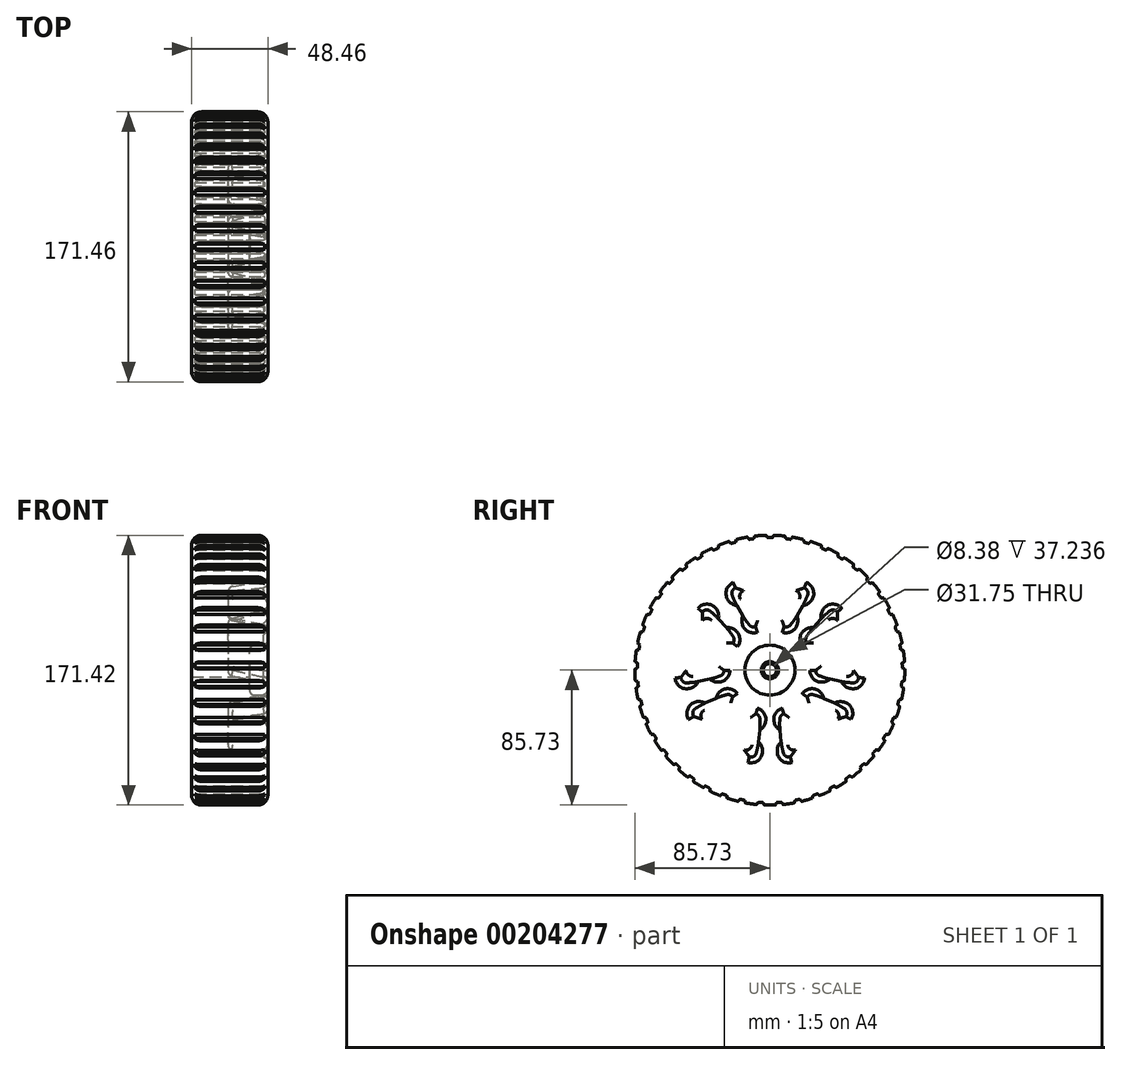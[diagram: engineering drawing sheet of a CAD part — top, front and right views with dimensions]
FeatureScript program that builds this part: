
annotation { "Feature Type Name" : "Feature", "Feature Type Description" : "" }
export const myFeature = defineFeature(function(context is Context, id is Id, definition is map)
    precondition{}
    {
        {
            var Q0;
            Q0=qCreatedBy(makeId("Front.planeOp"),FACE);
            var sketch = newSketch(context, id + "F0", { "sketchPlane" : qUnion([Q0])});
            skLineSegment(sketch, "E0", {"start": v(0, 85.73) * mm, "end": v(17.78, 85.73) * mm});
            skLineSegment(sketch, "E1", {"start": v(24.13, 79.38) * mm, "end": v(24.13, 19.05) * mm});
            skLineSegment(sketch, "E2", {"start": v(20.96, 15.88) * mm, "end": v(15.67, 15.88) * mm});
            skLineSegment(sketch, "E3", {"start": v(12.5, 12.7) * mm, "end": v(12.5, 5.46) * mm});
            skLineSegment(sketch, "E4", {"start": v(27.52, 0) * mm, "end": v(-27.22, 0) * mm});
            skLineSegment(sketch, "E5", {"start": v(0, 85.73) * mm, "end": v(-17.98, 85.73) * mm});
            skLineSegment(sketch, "E6", {"start": v(-24.33, 79.38) * mm, "end": v(-24.33, 4.2) * mm});
            skLineSegment(sketch, "E7", {"start": v(-24.33, 4.2) * mm, "end": v(12.9, 4.2) * mm});
            skPoint(sketch, "E8.end.orphan", {"position": v(0, 7.03) * mm});
            skLineSegment(sketch, "E9", {"start": v(12.5, 5.46) * mm, "end": v(12.9, 5.46) * mm});
            skLineSegment(sketch, "E10", {"start": v(12.9, 5.46) * mm, "end": v(12.9, 4.2) * mm});
            skPoint(sketch, "E11.visualSharp", {"position": v(-24.33, 85.73) * mm});
            skArc(sketch, "E11.filletArc", {"start": v(-17.98, 85.73) * mm, "mid": v(-22.47, 83.87) * mm, "end": v(-24.33, 79.38) * mm});
            skPoint(sketch, "E12.visualSharp", {"position": v(24.13, 85.73) * mm});
            skArc(sketch, "E12.filletArc", {"start": v(24.13, 79.38) * mm, "mid": v(22.27, 83.87) * mm, "end": v(17.78, 85.73) * mm});
            skPoint(sketch, "E13.visualSharp", {"position": v(24.13, 15.88) * mm});
            skArc(sketch, "E13.filletArc", {"start": v(20.96, 15.88) * mm, "mid": v(23.2, 16.8) * mm, "end": v(24.13, 19.05) * mm});
            skPoint(sketch, "E14.visualSharp", {"position": v(12.5, 15.88) * mm});
            skArc(sketch, "E14.filletArc", {"start": v(15.67, 15.88) * mm, "mid": v(13.43, 14.95) * mm, "end": v(12.5, 12.7) * mm});
            skSolve(sketch);
        }
        {
            var Q0;
            Q0=makeQuery(id+"F0.imprint","IMPRINT",FACE,{"disambiguationData":[TD([[makeQuery(id+"F0.imprint","IMPRINT",EDGE,{"derivedFrom":sQuery(id+"F0.wireOp",EDGE,"E0")}),-1.0]])]});
            var Q1;
            Q1=sQuery(id+"F0.wireOp",EDGE,"E4");
            revolve(context, id + "F1", {"entities" : qUnion([Q0]), "axis" : qUnion([Q1]), "revolveType" : RevolveType.FULL});
        }
        {
            var Q0;
            Q0=makeQuery(id+"F1.opRevolve","SWEPT_FACE",FACE,{"disambiguationData":[OSD([sQuery(id+"F0.wireOp",EDGE,"E1")])]});
            var sketch = newSketch(context, id + "F2", { "sketchPlane" : qUnion([Q0])});
            skArc(sketch, "E15", {"start": v(12.14, 25.87) * mm, "mid": v(0, 28.58) * mm, "end": v(-12.14, 25.87) * mm});
            skArc(sketch, "E16", {"start": v(26.46, 50.66) * mm, "mid": v(0, 57.15) * mm, "end": v(-26.46, 50.66) * mm});
            skLineSegment(sketch, "E17", {"start": v(-12.14, 25.87) * mm, "end": v(-26.46, 50.66) * mm});
            skLineSegment(sketch, "E18", {"start": v(12.14, 25.87) * mm, "end": v(26.46, 50.66) * mm});
            skPoint(sketch, "E19.visualSharp", {"position": v(-26.46, 50.66) * mm});
            skPoint(sketch, "E20.visualSharp", {"position": v(26.46, 50.66) * mm});
            skPoint(sketch, "E21.visualSharp", {"position": v(12.14, 25.87) * mm});
            skPoint(sketch, "E22.visualSharp", {"position": v(-12.14, 25.87) * mm});
            skLineSegment(sketch, "E23.1.0", {"start": v(-28.35, -3.56) * mm, "end": v(-56.35, -9.5) * mm});
            skArc(sketch, "E23.1.1", {"start": v(-40, 40.82) * mm, "mid": v(-54.35, 17.66) * mm, "end": v(-56.35, -9.5) * mm});
            skLineSegment(sketch, "E23.1.2", {"start": v(-20.85, 19.54) * mm, "end": v(-40, 40.82) * mm});
            skArc(sketch, "E23.1.3", {"start": v(-20.85, 19.54) * mm, "mid": v(-27.18, 8.83) * mm, "end": v(-28.35, -3.56) * mm});
            skLineSegment(sketch, "E23.2.0", {"start": v(-5.38, -28.06) * mm, "end": v(-8.37, -56.53) * mm});
            skArc(sketch, "E23.2.1", {"start": v(-51.18, -25.43) * mm, "mid": v(-33.6, -46.24) * mm, "end": v(-8.37, -56.53) * mm});
            skLineSegment(sketch, "E23.2.2", {"start": v(-25.03, -13.79) * mm, "end": v(-51.18, -25.43) * mm});
            skArc(sketch, "E23.2.3", {"start": v(-25.03, -13.79) * mm, "mid": v(-16.8, -23.12) * mm, "end": v(-5.38, -28.06) * mm});
            skLineSegment(sketch, "E23.3.0", {"start": v(25.03, -13.79) * mm, "end": v(51.18, -25.43) * mm});
            skArc(sketch, "E23.3.1", {"start": v(8.37, -56.53) * mm, "mid": v(33.6, -46.24) * mm, "end": v(51.18, -25.43) * mm});
            skLineSegment(sketch, "E23.3.2", {"start": v(5.38, -28.06) * mm, "end": v(8.37, -56.53) * mm});
            skArc(sketch, "E23.3.3", {"start": v(5.38, -28.06) * mm, "mid": v(16.8, -23.12) * mm, "end": v(25.03, -13.79) * mm});
            skLineSegment(sketch, "E23.4.0", {"start": v(20.85, 19.54) * mm, "end": v(40, 40.82) * mm});
            skArc(sketch, "E23.4.1", {"start": v(56.35, -9.5) * mm, "mid": v(54.35, 17.66) * mm, "end": v(40, 40.82) * mm});
            skLineSegment(sketch, "E23.4.2", {"start": v(28.35, -3.56) * mm, "end": v(56.35, -9.5) * mm});
            skArc(sketch, "E23.4.3", {"start": v(28.35, -3.56) * mm, "mid": v(27.18, 8.83) * mm, "end": v(20.85, 19.54) * mm});
            skSolve(sketch);
        }
        {
            var Q0;
            Q0=qSketchRegion(id+"F2",true);
            extrude(context, id + "F3", {"entities" : qUnion([Q0]), "operationType" : NewBodyOperationType.REMOVE, "oppositeDirection" : true, "depth" : 25.4 * mm, "hasDraft" : true, "draftAngle" : 10 * degree, "draftPullDirection" : true});
        }
        {
            var Q0;
            Q0=makeQuery(id+"F3.boolean.opBoolean","COPY",FACE,{"derivedFrom":makeQuery(id+"F3.opExtrude","SWEPT_FACE",FACE,{"disambiguationData":[OSD([sQuery(id+"F2.wireOp",EDGE,"E16")])]})});
            var Q1;
            Q1=makeQuery(id+"F3.boolean.opBoolean","COPY",FACE,{"derivedFrom":makeQuery(id+"F3.opExtrude","SWEPT_FACE",FACE,{"disambiguationData":[OSD([sQuery(id+"F2.wireOp",EDGE,"E15")])]})});
            var Q2;
            Q2=makeQuery(id+"F3.boolean.opBoolean","COPY",FACE,{"derivedFrom":makeQuery(id+"F3.opExtrude","CAP_FACE",FACE,{"disambiguationData":[OSD([sQuery(id+"F2.wireOp",EDGE,"E15"),sQuery(id+"F2.wireOp",EDGE,"E16"),sQuery(id+"F2.wireOp",EDGE,"E17"),sQuery(id+"F2.wireOp",EDGE,"E18")])],"isStart":false})});
            var Q3;
            Q3=makeQuery(id+"F3.boolean.opBoolean","COPY",FACE,{"derivedFrom":makeQuery(id+"F3.opExtrude","CAP_FACE",FACE,{"disambiguationData":[OSD([sQuery(id+"F2.wireOp",EDGE,"E23.1.0"),sQuery(id+"F2.wireOp",EDGE,"E23.1.1"),sQuery(id+"F2.wireOp",EDGE,"E23.1.2"),sQuery(id+"F2.wireOp",EDGE,"E23.1.3")])],"isStart":false})});
            var Q4;
            Q4=makeQuery(id+"F3.boolean.opBoolean","COPY",FACE,{"derivedFrom":makeQuery(id+"F3.opExtrude","SWEPT_FACE",FACE,{"disambiguationData":[OSD([sQuery(id+"F2.wireOp",EDGE,"E23.1.1")])]})});
            var Q5;
            Q5=makeQuery(id+"F3.boolean.opBoolean","COPY",FACE,{"derivedFrom":makeQuery(id+"F3.opExtrude","SWEPT_FACE",FACE,{"disambiguationData":[OSD([sQuery(id+"F2.wireOp",EDGE,"E23.1.3")])]})});
            var Q6;
            Q6=makeQuery(id+"F3.boolean.opBoolean","COPY",FACE,{"derivedFrom":makeQuery(id+"F3.opExtrude","CAP_FACE",FACE,{"disambiguationData":[OSD([sQuery(id+"F2.wireOp",EDGE,"E23.3.0"),sQuery(id+"F2.wireOp",EDGE,"E23.3.1"),sQuery(id+"F2.wireOp",EDGE,"E23.3.2"),sQuery(id+"F2.wireOp",EDGE,"E23.3.3")])],"isStart":false})});
            var Q7;
            Q7=makeQuery(id+"F3.boolean.opBoolean","COPY",FACE,{"derivedFrom":makeQuery(id+"F3.opExtrude","CAP_FACE",FACE,{"disambiguationData":[OSD([sQuery(id+"F2.wireOp",EDGE,"E23.2.0"),sQuery(id+"F2.wireOp",EDGE,"E23.2.1"),sQuery(id+"F2.wireOp",EDGE,"E23.2.2"),sQuery(id+"F2.wireOp",EDGE,"E23.2.3")])],"isStart":false})});
            var Q8;
            Q8=makeQuery(id+"F3.boolean.opBoolean","COPY",FACE,{"derivedFrom":makeQuery(id+"F3.opExtrude","SWEPT_FACE",FACE,{"disambiguationData":[OSD([sQuery(id+"F2.wireOp",EDGE,"E23.2.3")])]})});
            var Q9;
            Q9=makeQuery(id+"F3.boolean.opBoolean","COPY",FACE,{"derivedFrom":makeQuery(id+"F3.opExtrude","SWEPT_FACE",FACE,{"disambiguationData":[OSD([sQuery(id+"F2.wireOp",EDGE,"E23.3.3")])]})});
            var Q10;
            Q10=makeQuery(id+"F3.boolean.opBoolean","COPY",FACE,{"derivedFrom":makeQuery(id+"F3.opExtrude","SWEPT_FACE",FACE,{"disambiguationData":[OSD([sQuery(id+"F2.wireOp",EDGE,"E23.4.3")])]})});
            var Q11;
            Q11=makeQuery(id+"F3.boolean.opBoolean","COPY",FACE,{"derivedFrom":makeQuery(id+"F3.opExtrude","CAP_FACE",FACE,{"disambiguationData":[OSD([sQuery(id+"F2.wireOp",EDGE,"E23.4.0"),sQuery(id+"F2.wireOp",EDGE,"E23.4.1"),sQuery(id+"F2.wireOp",EDGE,"E23.4.2"),sQuery(id+"F2.wireOp",EDGE,"E23.4.3")])],"isStart":false})});
            var Q12;
            Q12=makeQuery(id+"F3.boolean.opBoolean","COPY",FACE,{"derivedFrom":makeQuery(id+"F3.opExtrude","SWEPT_FACE",FACE,{"disambiguationData":[OSD([sQuery(id+"F2.wireOp",EDGE,"E23.4.1")])]})});
            var Q13;
            Q13=makeQuery(id+"F3.boolean.opBoolean","COPY",FACE,{"derivedFrom":makeQuery(id+"F3.opExtrude","SWEPT_FACE",FACE,{"disambiguationData":[OSD([sQuery(id+"F2.wireOp",EDGE,"E23.3.1")])]})});
            var Q14;
            Q14=makeQuery(id+"F3.boolean.opBoolean","COPY",FACE,{"derivedFrom":makeQuery(id+"F3.opExtrude","SWEPT_FACE",FACE,{"disambiguationData":[OSD([sQuery(id+"F2.wireOp",EDGE,"E23.2.1")])]})});
            fillet(context, id + "F4", {"entities" : qUnion([Q0, Q1, Q2, Q3, Q4, Q5, Q6, Q7, Q8, Q9, Q10, Q11, Q12, Q13, Q14]), "radius" : 3.8 * mm, "tangentPropagation" : true, "allowEdgeOverflow" : false});
        }
        {
            var Q0;
            Q0=qCreatedBy(makeId("Right.planeOp"),FACE);
            var sketch = newSketch(context, id + "F5", { "sketchPlane" : qUnion([Q0])});
            skLineSegment(sketch, "E24", {"start": v(-1.59, 84.14) * mm, "end": v(1.59, 84.14) * mm});
            skLineSegment(sketch, "E25", {"start": v(-1.59, 84.14) * mm, "end": v(-3.18, 87.34) * mm});
            skLineSegment(sketch, "E26", {"start": v(1.59, 84.14) * mm, "end": v(3.17, 87.34) * mm});
            skLineSegment(sketch, "E27", {"start": v(-3.18, 87.34) * mm, "end": v(3.18, 87.34) * mm});
            skLineSegment(sketch, "E28.1.0", {"start": v(-15.3, 86.05) * mm, "end": v(-9.01, 86.94) * mm});
            skLineSegment(sketch, "E28.1.1", {"start": v(-13.28, 83.1) * mm, "end": v(-10.14, 83.54) * mm});
            skLineSegment(sketch, "E28.1.2", {"start": v(-10.14, 83.54) * mm, "end": v(-9.01, 86.94) * mm});
            skLineSegment(sketch, "E28.1.3", {"start": v(-13.28, 83.1) * mm, "end": v(-15.3, 86.05) * mm});
            skLineSegment(sketch, "E28.2.0", {"start": v(-27.13, 83.09) * mm, "end": v(-21.02, 84.84) * mm});
            skLineSegment(sketch, "E28.2.1", {"start": v(-24.72, 80.44) * mm, "end": v(-21.67, 81.32) * mm});
            skLineSegment(sketch, "E28.2.2", {"start": v(-21.67, 81.32) * mm, "end": v(-21.02, 84.84) * mm});
            skLineSegment(sketch, "E28.2.3", {"start": v(-24.72, 80.44) * mm, "end": v(-27.13, 83.09) * mm});
            skLineSegment(sketch, "E28.3.0", {"start": v(-38.43, 78.5) * mm, "end": v(-32.63, 81.08) * mm});
            skLineSegment(sketch, "E28.3.1", {"start": v(-35.67, 76.22) * mm, "end": v(-32.77, 77.5) * mm});
            skLineSegment(sketch, "E28.3.2", {"start": v(-32.77, 77.5) * mm, "end": v(-32.63, 81.08) * mm});
            skLineSegment(sketch, "E28.3.3", {"start": v(-35.67, 76.22) * mm, "end": v(-38.43, 78.5) * mm});
            skLineSegment(sketch, "E28.4.0", {"start": v(-48.98, 72.4) * mm, "end": v(-43.6, 75.76) * mm});
            skLineSegment(sketch, "E28.4.1", {"start": v(-45.93, 70.51) * mm, "end": v(-43.24, 72.2) * mm});
            skLineSegment(sketch, "E28.4.2", {"start": v(-43.24, 72.2) * mm, "end": v(-43.6, 75.76) * mm});
            skLineSegment(sketch, "E28.4.3", {"start": v(-45.93, 70.51) * mm, "end": v(-48.98, 72.4) * mm});
            skLineSegment(sketch, "E28.5.0", {"start": v(-58.58, 64.87) * mm, "end": v(-53.71, 68.95) * mm});
            skLineSegment(sketch, "E28.5.1", {"start": v(-55.3, 63.43) * mm, "end": v(-52.87, 65.47) * mm});
            skLineSegment(sketch, "E28.5.2", {"start": v(-52.87, 65.47) * mm, "end": v(-53.71, 68.95) * mm});
            skLineSegment(sketch, "E28.5.3", {"start": v(-55.3, 63.43) * mm, "end": v(-58.58, 64.87) * mm});
            skLineSegment(sketch, "E28.6.0", {"start": v(-67.03, 56.09) * mm, "end": v(-62.79, 60.8) * mm});
            skLineSegment(sketch, "E28.6.1", {"start": v(-63.59, 55.12) * mm, "end": v(-61.46, 57.48) * mm});
            skLineSegment(sketch, "E28.6.2", {"start": v(-61.46, 57.48) * mm, "end": v(-62.79, 60.8) * mm});
            skLineSegment(sketch, "E28.6.3", {"start": v(-63.59, 55.12) * mm, "end": v(-67.03, 56.09) * mm});
            skLineSegment(sketch, "E28.7.0", {"start": v(-74.19, 46.21) * mm, "end": v(-70.64, 51.47) * mm});
            skLineSegment(sketch, "E28.7.1", {"start": v(-70.64, 45.73) * mm, "end": v(-68.87, 48.37) * mm});
            skLineSegment(sketch, "E28.7.2", {"start": v(-68.87, 48.37) * mm, "end": v(-70.64, 51.47) * mm});
            skLineSegment(sketch, "E28.7.3", {"start": v(-70.64, 45.73) * mm, "end": v(-74.19, 46.21) * mm});
            skLineSegment(sketch, "E28.8.0", {"start": v(-79.9, 35.44) * mm, "end": v(-77.11, 41.14) * mm});
            skLineSegment(sketch, "E28.8.1", {"start": v(-76.32, 35.46) * mm, "end": v(-74.93, 38.31) * mm});
            skLineSegment(sketch, "E28.8.2", {"start": v(-74.93, 38.31) * mm, "end": v(-77.11, 41.14) * mm});
            skLineSegment(sketch, "E28.8.3", {"start": v(-76.32, 35.46) * mm, "end": v(-79.9, 35.44) * mm});
            skLineSegment(sketch, "E28.9.0", {"start": v(-84.05, 23.97) * mm, "end": v(-82.09, 30.01) * mm});
            skLineSegment(sketch, "E28.9.1", {"start": v(-80.51, 24.5) * mm, "end": v(-79.53, 27.5) * mm});
            skLineSegment(sketch, "E28.9.2", {"start": v(-79.53, 27.5) * mm, "end": v(-82.09, 30.01) * mm});
            skLineSegment(sketch, "E28.9.3", {"start": v(-80.51, 24.5) * mm, "end": v(-84.05, 23.97) * mm});
            skLineSegment(sketch, "E28.10.0", {"start": v(-86.57, 12.04) * mm, "end": v(-85.47, 18.3) * mm});
            skLineSegment(sketch, "E28.10.1", {"start": v(-83.13, 13.05) * mm, "end": v(-82.58, 16.17) * mm});
            skLineSegment(sketch, "E28.10.2", {"start": v(-82.58, 16.17) * mm, "end": v(-85.47, 18.3) * mm});
            skLineSegment(sketch, "E28.10.3", {"start": v(-83.13, 13.05) * mm, "end": v(-86.57, 12.04) * mm});
            skLineSegment(sketch, "E28.11.0", {"start": v(-87.4, -0.12) * mm, "end": v(-87.18, 6.22) * mm});
            skLineSegment(sketch, "E28.11.1", {"start": v(-84.14, 1.35) * mm, "end": v(-84.03, 4.52) * mm});
            skLineSegment(sketch, "E28.11.2", {"start": v(-84.03, 4.52) * mm, "end": v(-87.18, 6.22) * mm});
            skLineSegment(sketch, "E28.11.3", {"start": v(-84.14, 1.35) * mm, "end": v(-87.4, -0.12) * mm});
            skLineSegment(sketch, "E28.12.0", {"start": v(-86.53, -12.29) * mm, "end": v(-87.2, -5.97) * mm});
            skLineSegment(sketch, "E28.12.1", {"start": v(-83.51, -10.37) * mm, "end": v(-83.84, -7.22) * mm});
            skLineSegment(sketch, "E28.12.2", {"start": v(-83.84, -7.22) * mm, "end": v(-87.2, -5.97) * mm});
            skLineSegment(sketch, "E28.12.3", {"start": v(-83.51, -10.37) * mm, "end": v(-86.53, -12.29) * mm});
            skLineSegment(sketch, "E28.13.0", {"start": v(-83.98, -24.21) * mm, "end": v(-85.52, -18.05) * mm});
            skLineSegment(sketch, "E28.13.1", {"start": v(-81.25, -21.9) * mm, "end": v(-82.02, -18.81) * mm});
            skLineSegment(sketch, "E28.13.2", {"start": v(-82.02, -18.81) * mm, "end": v(-85.52, -18.05) * mm});
            skLineSegment(sketch, "E28.13.3", {"start": v(-81.25, -21.9) * mm, "end": v(-83.98, -24.21) * mm});
            skLineSegment(sketch, "E28.14.0", {"start": v(-79.8, -35.66) * mm, "end": v(-82.17, -29.78) * mm});
            skLineSegment(sketch, "E28.14.1", {"start": v(-77.42, -33) * mm, "end": v(-78.6, -30.05) * mm});
            skLineSegment(sketch, "E28.14.2", {"start": v(-78.6, -30.05) * mm, "end": v(-82.17, -29.78) * mm});
            skLineSegment(sketch, "E28.14.3", {"start": v(-77.42, -33) * mm, "end": v(-79.8, -35.66) * mm});
            skLineSegment(sketch, "E28.15.0", {"start": v(-74.06, -46.42) * mm, "end": v(-77.23, -40.92) * mm});
            skLineSegment(sketch, "E28.15.1", {"start": v(-72.07, -43.44) * mm, "end": v(-73.66, -40.7) * mm});
            skLineSegment(sketch, "E28.15.2", {"start": v(-73.66, -40.7) * mm, "end": v(-77.23, -40.92) * mm});
            skLineSegment(sketch, "E28.15.3", {"start": v(-72.07, -43.44) * mm, "end": v(-74.06, -46.42) * mm});
            skLineSegment(sketch, "E28.16.0", {"start": v(-66.87, -56.28) * mm, "end": v(-70.78, -51.27) * mm});
            skLineSegment(sketch, "E28.16.1", {"start": v(-65.32, -53.05) * mm, "end": v(-67.28, -50.55) * mm});
            skLineSegment(sketch, "E28.16.2", {"start": v(-67.28, -50.55) * mm, "end": v(-70.78, -51.27) * mm});
            skLineSegment(sketch, "E28.16.3", {"start": v(-65.32, -53.05) * mm, "end": v(-66.87, -56.28) * mm});
            skLineSegment(sketch, "E28.17.0", {"start": v(-58.4, -65.04) * mm, "end": v(-62.96, -60.63) * mm});
            skLineSegment(sketch, "E28.17.1", {"start": v(-57.3, -61.63) * mm, "end": v(-59.59, -59.42) * mm});
            skLineSegment(sketch, "E28.17.2", {"start": v(-59.59, -59.42) * mm, "end": v(-62.96, -60.63) * mm});
            skLineSegment(sketch, "E28.17.3", {"start": v(-57.3, -61.63) * mm, "end": v(-58.4, -65.04) * mm});
            skLineSegment(sketch, "E28.18.0", {"start": v(-48.77, -72.53) * mm, "end": v(-53.9, -68.8) * mm});
            skLineSegment(sketch, "E28.18.1", {"start": v(-48.17, -69) * mm, "end": v(-50.74, -67.14) * mm});
            skLineSegment(sketch, "E28.18.2", {"start": v(-50.74, -67.14) * mm, "end": v(-53.9, -68.8) * mm});
            skLineSegment(sketch, "E28.18.3", {"start": v(-48.17, -69) * mm, "end": v(-48.77, -72.53) * mm});
            skLineSegment(sketch, "E28.19.0", {"start": v(-38.2, -78.61) * mm, "end": v(-43.8, -75.63) * mm});
            skLineSegment(sketch, "E28.19.1", {"start": v(-38.1, -75.03) * mm, "end": v(-40.9, -73.54) * mm});
            skLineSegment(sketch, "E28.19.2", {"start": v(-40.9, -73.54) * mm, "end": v(-43.8, -75.63) * mm});
            skLineSegment(sketch, "E28.19.3", {"start": v(-38.1, -75.03) * mm, "end": v(-38.2, -78.61) * mm});
            skLineSegment(sketch, "E28.20.0", {"start": v(-26.9, -83.16) * mm, "end": v(-32.86, -81) * mm});
            skLineSegment(sketch, "E28.20.1", {"start": v(-27.28, -79.6) * mm, "end": v(-30.27, -78.52) * mm});
            skLineSegment(sketch, "E28.20.2", {"start": v(-30.27, -78.52) * mm, "end": v(-32.86, -81) * mm});
            skLineSegment(sketch, "E28.20.3", {"start": v(-27.28, -79.6) * mm, "end": v(-26.9, -83.16) * mm});
            skLineSegment(sketch, "E28.21.0", {"start": v(-15.05, -86.1) * mm, "end": v(-21.27, -84.78) * mm});
            skLineSegment(sketch, "E28.21.1", {"start": v(-15.94, -82.63) * mm, "end": v(-19.05, -81.97) * mm});
            skLineSegment(sketch, "E28.21.2", {"start": v(-19.05, -81.97) * mm, "end": v(-21.27, -84.78) * mm});
            skLineSegment(sketch, "E28.21.3", {"start": v(-15.94, -82.63) * mm, "end": v(-15.05, -86.1) * mm});
            skLineSegment(sketch, "E28.22.0", {"start": v(-2.93, -87.35) * mm, "end": v(-9.26, -86.91) * mm});
            skLineSegment(sketch, "E28.22.1", {"start": v(-4.29, -84.04) * mm, "end": v(-7.45, -83.82) * mm});
            skLineSegment(sketch, "E28.22.2", {"start": v(-7.45, -83.82) * mm, "end": v(-9.26, -86.91) * mm});
            skLineSegment(sketch, "E28.22.3", {"start": v(-4.29, -84.04) * mm, "end": v(-2.93, -87.35) * mm});
            skLineSegment(sketch, "E28.23.0", {"start": v(9.26, -86.91) * mm, "end": v(2.93, -87.35) * mm});
            skLineSegment(sketch, "E28.23.1", {"start": v(7.45, -83.82) * mm, "end": v(4.29, -84.04) * mm});
            skLineSegment(sketch, "E28.23.2", {"start": v(4.29, -84.04) * mm, "end": v(2.93, -87.35) * mm});
            skLineSegment(sketch, "E28.23.3", {"start": v(7.45, -83.82) * mm, "end": v(9.26, -86.91) * mm});
            skLineSegment(sketch, "E28.24.0", {"start": v(21.27, -84.78) * mm, "end": v(15.05, -86.1) * mm});
            skLineSegment(sketch, "E28.24.1", {"start": v(19.05, -81.97) * mm, "end": v(15.94, -82.63) * mm});
            skLineSegment(sketch, "E28.24.2", {"start": v(15.94, -82.63) * mm, "end": v(15.05, -86.1) * mm});
            skLineSegment(sketch, "E28.24.3", {"start": v(19.05, -81.97) * mm, "end": v(21.27, -84.78) * mm});
            skPoint(sketch, "E28.center", {"position": v(0, 0) * mm});
            skLineSegment(sketch, "E29.1.25.0", {"start": v(32.86, -81) * mm, "end": v(26.9, -83.16) * mm});
            skLineSegment(sketch, "E29.3.25.0", {"start": v(30.27, -78.52) * mm, "end": v(27.28, -79.6) * mm});
            skLineSegment(sketch, "E29.6.25.0", {"start": v(27.28, -79.6) * mm, "end": v(26.9, -83.16) * mm});
            skLineSegment(sketch, "E29.9.25.0", {"start": v(30.27, -78.52) * mm, "end": v(32.86, -81) * mm});
            skLineSegment(sketch, "E29.1.26.0", {"start": v(43.8, -75.63) * mm, "end": v(38.2, -78.61) * mm});
            skLineSegment(sketch, "E29.3.26.0", {"start": v(40.9, -73.54) * mm, "end": v(38.1, -75.03) * mm});
            skLineSegment(sketch, "E29.6.26.0", {"start": v(38.1, -75.03) * mm, "end": v(38.2, -78.61) * mm});
            skLineSegment(sketch, "E29.9.26.0", {"start": v(40.9, -73.54) * mm, "end": v(43.8, -75.63) * mm});
            skLineSegment(sketch, "E29.1.27.0", {"start": v(53.9, -68.8) * mm, "end": v(48.77, -72.53) * mm});
            skLineSegment(sketch, "E29.3.27.0", {"start": v(50.74, -67.14) * mm, "end": v(48.17, -69) * mm});
            skLineSegment(sketch, "E29.6.27.0", {"start": v(48.17, -69) * mm, "end": v(48.77, -72.53) * mm});
            skLineSegment(sketch, "E29.9.27.0", {"start": v(50.74, -67.14) * mm, "end": v(53.9, -68.8) * mm});
            skLineSegment(sketch, "E29.1.28.0", {"start": v(62.96, -60.63) * mm, "end": v(58.4, -65.04) * mm});
            skLineSegment(sketch, "E29.3.28.0", {"start": v(59.59, -59.42) * mm, "end": v(57.3, -61.63) * mm});
            skLineSegment(sketch, "E29.6.28.0", {"start": v(57.3, -61.63) * mm, "end": v(58.4, -65.04) * mm});
            skLineSegment(sketch, "E29.9.28.0", {"start": v(59.59, -59.42) * mm, "end": v(62.96, -60.63) * mm});
            skLineSegment(sketch, "E29.1.29.0", {"start": v(70.78, -51.27) * mm, "end": v(66.87, -56.28) * mm});
            skLineSegment(sketch, "E29.3.29.0", {"start": v(67.28, -50.55) * mm, "end": v(65.32, -53.05) * mm});
            skLineSegment(sketch, "E29.6.29.0", {"start": v(65.32, -53.05) * mm, "end": v(66.87, -56.28) * mm});
            skLineSegment(sketch, "E29.9.29.0", {"start": v(67.28, -50.55) * mm, "end": v(70.78, -51.27) * mm});
            skLineSegment(sketch, "E29.1.30.0", {"start": v(77.23, -40.92) * mm, "end": v(74.06, -46.42) * mm});
            skLineSegment(sketch, "E29.3.30.0", {"start": v(73.66, -40.7) * mm, "end": v(72.07, -43.44) * mm});
            skLineSegment(sketch, "E29.6.30.0", {"start": v(72.07, -43.44) * mm, "end": v(74.06, -46.42) * mm});
            skLineSegment(sketch, "E29.9.30.0", {"start": v(73.66, -40.7) * mm, "end": v(77.23, -40.92) * mm});
            skLineSegment(sketch, "E29.1.31.0", {"start": v(82.17, -29.78) * mm, "end": v(79.8, -35.66) * mm});
            skLineSegment(sketch, "E29.3.31.0", {"start": v(78.6, -30.05) * mm, "end": v(77.42, -33) * mm});
            skLineSegment(sketch, "E29.6.31.0", {"start": v(77.42, -33) * mm, "end": v(79.8, -35.66) * mm});
            skLineSegment(sketch, "E29.9.31.0", {"start": v(78.6, -30.05) * mm, "end": v(82.17, -29.78) * mm});
            skLineSegment(sketch, "E29.1.32.0", {"start": v(85.52, -18.05) * mm, "end": v(83.98, -24.21) * mm});
            skLineSegment(sketch, "E29.3.32.0", {"start": v(82.02, -18.81) * mm, "end": v(81.25, -21.9) * mm});
            skLineSegment(sketch, "E29.6.32.0", {"start": v(81.25, -21.9) * mm, "end": v(83.98, -24.21) * mm});
            skLineSegment(sketch, "E29.9.32.0", {"start": v(82.02, -18.81) * mm, "end": v(85.52, -18.05) * mm});
            skLineSegment(sketch, "E29.1.33.0", {"start": v(87.2, -5.97) * mm, "end": v(86.53, -12.29) * mm});
            skLineSegment(sketch, "E29.3.33.0", {"start": v(83.84, -7.22) * mm, "end": v(83.51, -10.37) * mm});
            skLineSegment(sketch, "E29.6.33.0", {"start": v(83.51, -10.37) * mm, "end": v(86.53, -12.29) * mm});
            skLineSegment(sketch, "E29.9.33.0", {"start": v(83.84, -7.22) * mm, "end": v(87.2, -5.97) * mm});
            skLineSegment(sketch, "E29.1.34.0", {"start": v(87.18, 6.22) * mm, "end": v(87.4, -0.12) * mm});
            skLineSegment(sketch, "E29.3.34.0", {"start": v(84.03, 4.52) * mm, "end": v(84.14, 1.35) * mm});
            skLineSegment(sketch, "E29.6.34.0", {"start": v(84.14, 1.35) * mm, "end": v(87.4, -0.12) * mm});
            skLineSegment(sketch, "E29.9.34.0", {"start": v(84.03, 4.52) * mm, "end": v(87.18, 6.22) * mm});
            skLineSegment(sketch, "E30.1.35.0", {"start": v(85.47, 18.3) * mm, "end": v(86.57, 12.04) * mm});
            skLineSegment(sketch, "E30.3.35.0", {"start": v(82.58, 16.17) * mm, "end": v(83.13, 13.05) * mm});
            skLineSegment(sketch, "E30.6.35.0", {"start": v(83.13, 13.05) * mm, "end": v(86.57, 12.04) * mm});
            skLineSegment(sketch, "E30.9.35.0", {"start": v(82.58, 16.17) * mm, "end": v(85.47, 18.3) * mm});
            skLineSegment(sketch, "E30.1.36.0", {"start": v(82.09, 30.01) * mm, "end": v(84.05, 23.97) * mm});
            skLineSegment(sketch, "E30.3.36.0", {"start": v(79.53, 27.5) * mm, "end": v(80.51, 24.5) * mm});
            skLineSegment(sketch, "E30.6.36.0", {"start": v(80.51, 24.5) * mm, "end": v(84.05, 23.97) * mm});
            skLineSegment(sketch, "E30.9.36.0", {"start": v(79.53, 27.5) * mm, "end": v(82.09, 30.01) * mm});
            skLineSegment(sketch, "E30.1.37.0", {"start": v(77.11, 41.14) * mm, "end": v(79.9, 35.44) * mm});
            skLineSegment(sketch, "E30.3.37.0", {"start": v(74.93, 38.31) * mm, "end": v(76.32, 35.46) * mm});
            skLineSegment(sketch, "E30.6.37.0", {"start": v(76.32, 35.46) * mm, "end": v(79.9, 35.44) * mm});
            skLineSegment(sketch, "E30.9.37.0", {"start": v(74.93, 38.31) * mm, "end": v(77.11, 41.14) * mm});
            skLineSegment(sketch, "E30.1.38.0", {"start": v(70.64, 51.47) * mm, "end": v(74.19, 46.21) * mm});
            skLineSegment(sketch, "E30.3.38.0", {"start": v(68.87, 48.37) * mm, "end": v(70.64, 45.73) * mm});
            skLineSegment(sketch, "E30.6.38.0", {"start": v(70.64, 45.73) * mm, "end": v(74.19, 46.21) * mm});
            skLineSegment(sketch, "E30.9.38.0", {"start": v(68.87, 48.37) * mm, "end": v(70.64, 51.47) * mm});
            skLineSegment(sketch, "E30.1.39.0", {"start": v(62.79, 60.8) * mm, "end": v(67.03, 56.09) * mm});
            skLineSegment(sketch, "E30.3.39.0", {"start": v(61.46, 57.48) * mm, "end": v(63.59, 55.12) * mm});
            skLineSegment(sketch, "E30.6.39.0", {"start": v(63.59, 55.12) * mm, "end": v(67.03, 56.09) * mm});
            skLineSegment(sketch, "E30.9.39.0", {"start": v(61.46, 57.48) * mm, "end": v(62.79, 60.8) * mm});
            skLineSegment(sketch, "E31.1.40.0", {"start": v(53.71, 68.95) * mm, "end": v(58.58, 64.87) * mm});
            skLineSegment(sketch, "E31.3.40.0", {"start": v(52.87, 65.47) * mm, "end": v(55.3, 63.43) * mm});
            skLineSegment(sketch, "E31.6.40.0", {"start": v(55.3, 63.43) * mm, "end": v(58.58, 64.87) * mm});
            skLineSegment(sketch, "E31.9.40.0", {"start": v(52.87, 65.47) * mm, "end": v(53.71, 68.95) * mm});
            skLineSegment(sketch, "E31.1.41.0", {"start": v(43.6, 75.76) * mm, "end": v(48.98, 72.4) * mm});
            skLineSegment(sketch, "E31.3.41.0", {"start": v(43.24, 72.2) * mm, "end": v(45.93, 70.51) * mm});
            skLineSegment(sketch, "E31.6.41.0", {"start": v(45.93, 70.51) * mm, "end": v(48.98, 72.4) * mm});
            skLineSegment(sketch, "E31.9.41.0", {"start": v(43.24, 72.2) * mm, "end": v(43.6, 75.76) * mm});
            skLineSegment(sketch, "E31.1.42.0", {"start": v(32.63, 81.08) * mm, "end": v(38.43, 78.5) * mm});
            skLineSegment(sketch, "E31.3.42.0", {"start": v(32.77, 77.5) * mm, "end": v(35.67, 76.22) * mm});
            skLineSegment(sketch, "E31.6.42.0", {"start": v(35.67, 76.22) * mm, "end": v(38.43, 78.5) * mm});
            skLineSegment(sketch, "E31.9.42.0", {"start": v(32.77, 77.5) * mm, "end": v(32.63, 81.08) * mm});
            skLineSegment(sketch, "E31.1.43.0", {"start": v(21.02, 84.84) * mm, "end": v(27.13, 83.09) * mm});
            skLineSegment(sketch, "E31.3.43.0", {"start": v(21.67, 81.32) * mm, "end": v(24.72, 80.44) * mm});
            skLineSegment(sketch, "E31.6.43.0", {"start": v(24.72, 80.44) * mm, "end": v(27.13, 83.09) * mm});
            skLineSegment(sketch, "E31.9.43.0", {"start": v(21.67, 81.32) * mm, "end": v(21.02, 84.84) * mm});
            skLineSegment(sketch, "E31.1.44.0", {"start": v(9.01, 86.94) * mm, "end": v(15.3, 86.05) * mm});
            skLineSegment(sketch, "E31.3.44.0", {"start": v(10.14, 83.54) * mm, "end": v(13.28, 83.1) * mm});
            skLineSegment(sketch, "E31.6.44.0", {"start": v(13.28, 83.1) * mm, "end": v(15.3, 86.05) * mm});
            skLineSegment(sketch, "E31.9.44.0", {"start": v(10.14, 83.54) * mm, "end": v(9.01, 86.94) * mm});
            skSolve(sketch);
        }
        {
            var Q0;
            Q0=qSketchRegion(id+"F5",true);
            extrude(context, id + "F6", {"entities" : qUnion([Q0]), "operationType" : NewBodyOperationType.REMOVE, "endBound" : BoundingType.SYMMETRIC, "oppositeDirection" : true, "depth" : 50.8 * mm});
        }
    });
